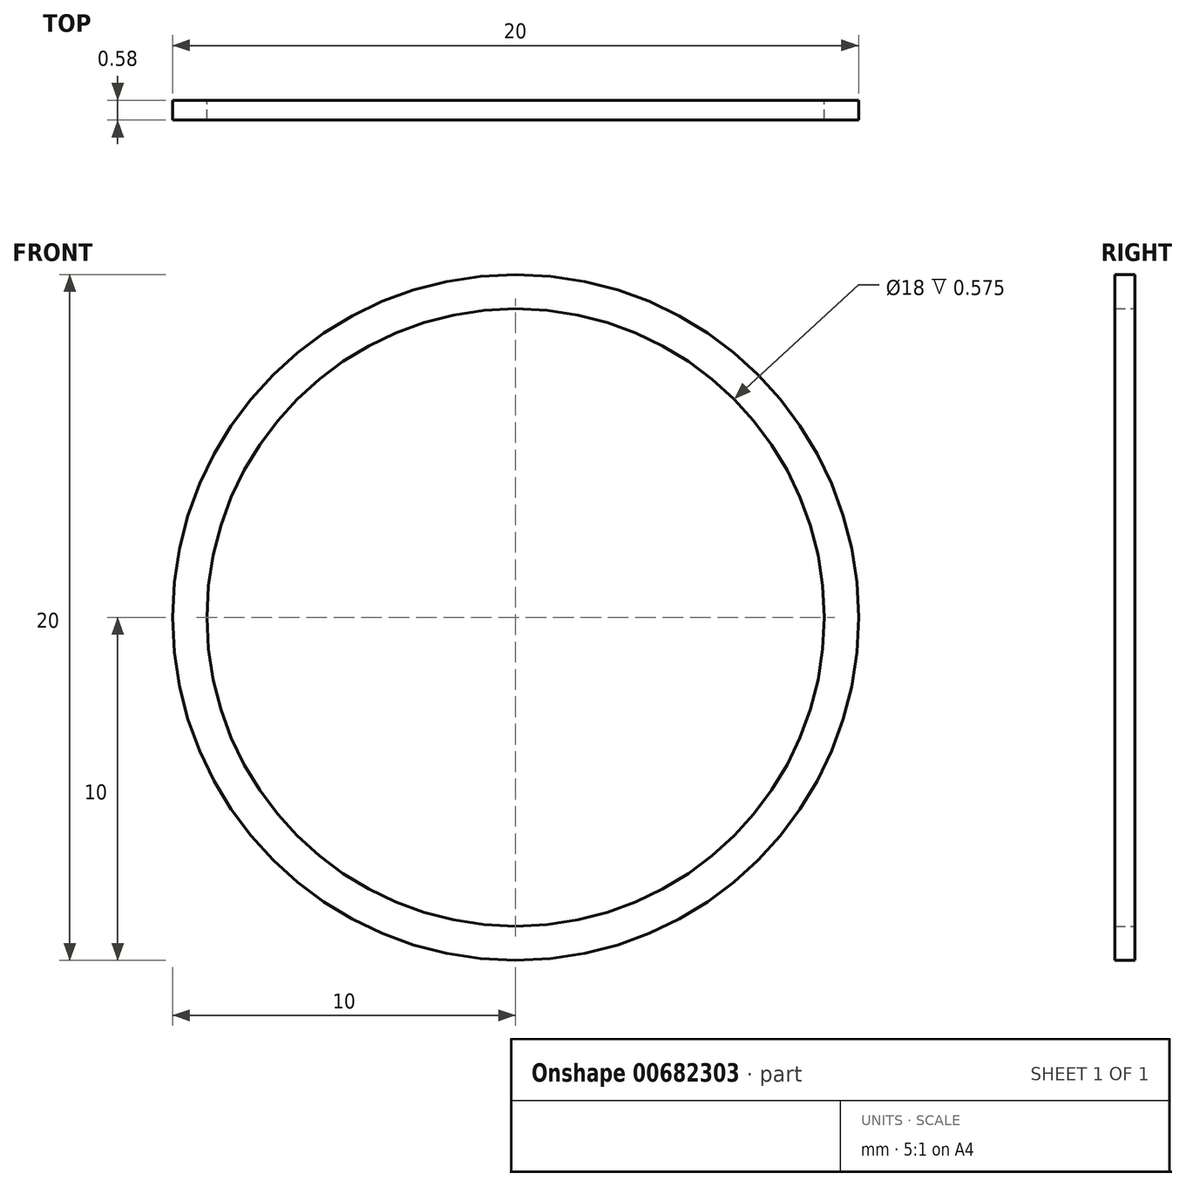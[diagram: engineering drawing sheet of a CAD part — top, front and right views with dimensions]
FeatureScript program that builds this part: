
annotation { "Feature Type Name" : "Feature", "Feature Type Description" : "" }
export const myFeature = defineFeature(function(context is Context, id is Id, definition is map)
    precondition{}
    {
        {
            var Q0;
            Q0=qCreatedBy(makeId("Front.planeOp"),FACE);
            var sketch = newSketch(context, id + "F0", { "sketchPlane" : qUnion([Q0])});
            skCircle(sketch, "E0", {"center": v(0, 0) * mm, "radius": 10 * mm});
            skCircle(sketch, "E1", {"center": v(0, 0) * mm, "radius": 9 * mm});
            skSolve(sketch);
        }
        {
            var Q0;
            Q0=makeQuery(id+"F0.imprint","IMPRINT",FACE,{"disambiguationData":[TD([[makeQuery(id+"F0.imprint","IMPRINT",EDGE,{"derivedFrom":sQuery(id+"F0.wireOp",EDGE,"E0")}),1.0]])]});
            extrude(context, id + "F1", {"entities" : qUnion([Q0]), "depth" : .575 * mm, "offsetDistance" : 25 * mm});
        }
    });
